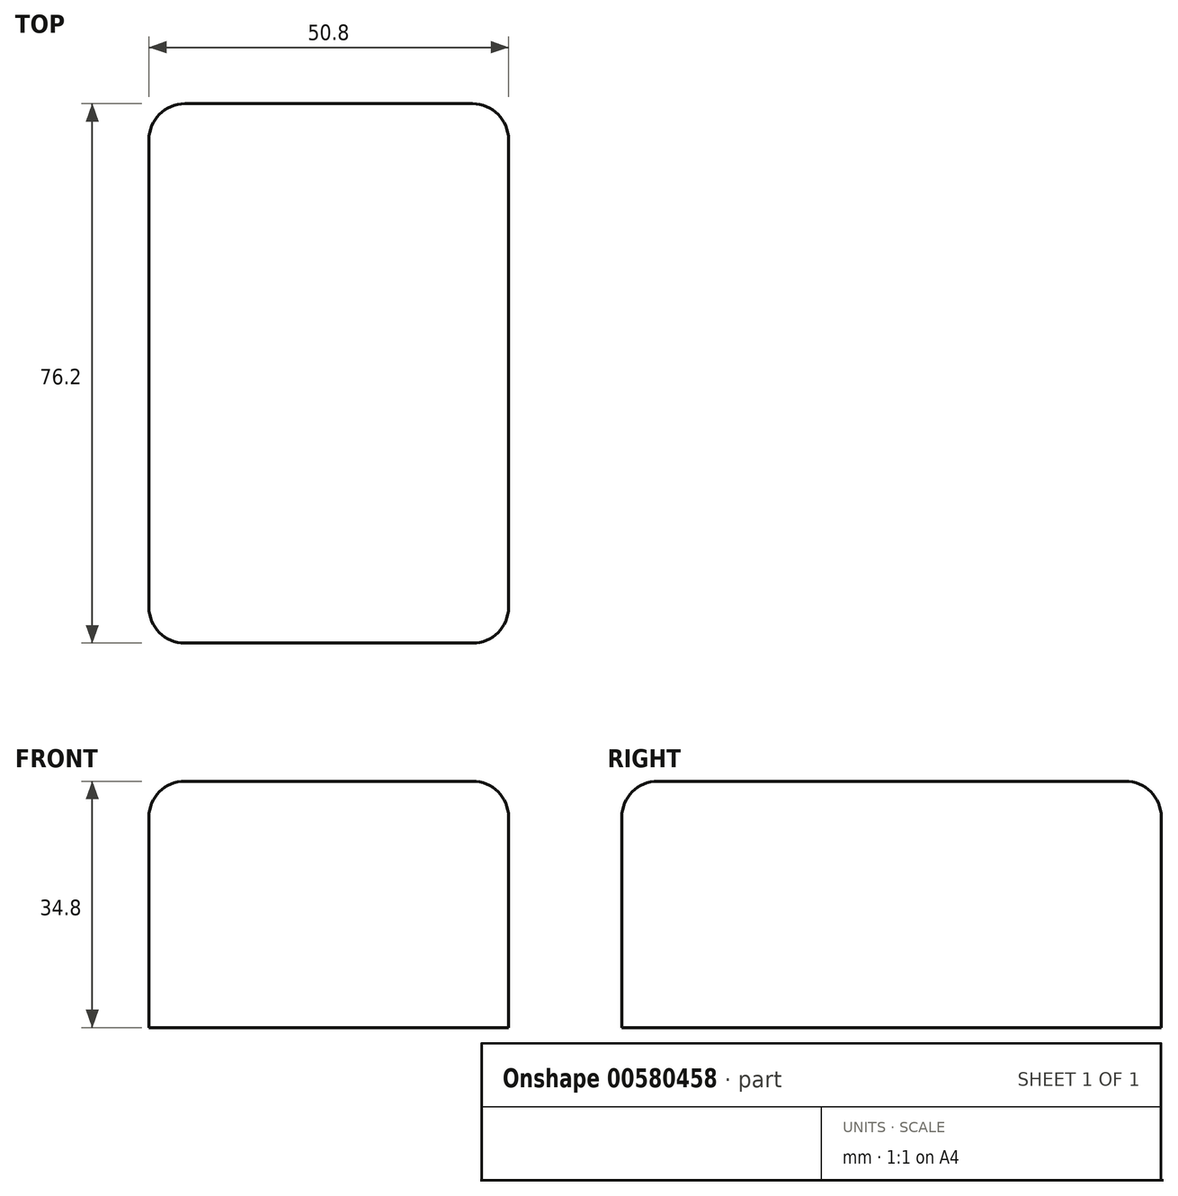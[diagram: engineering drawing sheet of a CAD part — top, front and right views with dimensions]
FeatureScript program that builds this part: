
annotation { "Feature Type Name" : "Feature", "Feature Type Description" : "" }
export const myFeature = defineFeature(function(context is Context, id is Id, definition is map)
    precondition{}
    {
        {
            var Q0;
            Q0=qCreatedBy(makeId("Top.planeOp"),FACE);
            var sketch = newSketch(context, id + "F0", { "sketchPlane" : qUnion([Q0])});
            skLineSegment(sketch, "E0.bottom", {"start": v(-25.4, 25.4) * mm, "end": v(25.4, 25.4) * mm});
            skLineSegment(sketch, "E0.top", {"start": v(-25.4, -50.8) * mm, "end": v(25.4, -50.8) * mm});
            skLineSegment(sketch, "E0.left", {"start": v(-25.4, 25.4) * mm, "end": v(-25.4, -50.8) * mm});
            skLineSegment(sketch, "E0.right", {"start": v(25.4, 25.4) * mm, "end": v(25.4, -50.8) * mm});
            skPoint(sketch, "E1.firstSnap0", {"position": v(0, 25.4) * mm});
            skSolve(sketch);
        }
        {
            var Q0;
            Q0=makeQuery(id+"F0.imprint","IMPRINT",FACE,{"disambiguationData":[TD([[makeQuery(id+"F0.imprint","IMPRINT",EDGE,{"derivedFrom":sQuery(id+"F0.wireOp",EDGE,"E0.bottom")}),-1.0]])]});
            extrude(context, id + "F1", {"entities" : qUnion([Q0]), "depth" : 34.8 * mm, "offsetDistance" : 25.4 * mm});
        }
        {
            var Q0;
            Q0=makeQuery(id+"F1.opExtrude","CAP_EDGE",EDGE,{"disambiguationData":[OSD([sQuery(id+"F0.wireOp",EDGE,"E0.left")])],"isStart":false});
            var Q1;
            Q1=makeQuery(id+"F1.opExtrude","CAP_EDGE",EDGE,{"disambiguationData":[OSD([sQuery(id+"F0.wireOp",EDGE,"E0.bottom")])],"isStart":false});
            var Q2;
            Q2=makeQuery(id+"F1.opExtrude","CAP_EDGE",EDGE,{"disambiguationData":[OSD([sQuery(id+"F0.wireOp",EDGE,"E0.right")])],"isStart":false});
            var Q3;
            Q3=makeQuery(id+"F1.opExtrude","CAP_FACE",FACE,{"disambiguationData":[OSD([sQuery(id+"F0.wireOp",EDGE,"E0.bottom"),sQuery(id+"F0.wireOp",EDGE,"E0.top"),sQuery(id+"F0.wireOp",EDGE,"E0.left"),sQuery(id+"F0.wireOp",EDGE,"E0.right")])],"isStart":false});
            var Q4;
            Q4=makeQuery(id+"F1.opExtrude","SWEPT_EDGE",EDGE,{"disambiguationData":[OSD([sQuery(id+"F0.wireOp",EDGE,"E0.top"),sQuery(id+"F0.wireOp",EDGE,"E0.right")])]});
            var Q5;
            Q5=makeQuery(id+"F1.opExtrude","SWEPT_EDGE",EDGE,{"disambiguationData":[OSD([sQuery(id+"F0.wireOp",EDGE,"E0.bottom"),sQuery(id+"F0.wireOp",EDGE,"E0.right")])]});
            var Q6;
            Q6=makeQuery(id+"F1.opExtrude","SWEPT_EDGE",EDGE,{"disambiguationData":[OSD([sQuery(id+"F0.wireOp",EDGE,"E0.bottom"),sQuery(id+"F0.wireOp",EDGE,"E0.left")])]});
            var Q7;
            Q7=makeQuery(id+"F1.opExtrude","SWEPT_EDGE",EDGE,{"disambiguationData":[OSD([sQuery(id+"F0.wireOp",EDGE,"E0.top"),sQuery(id+"F0.wireOp",EDGE,"E0.left")])]});
            fillet(context, id + "F2", {"entities" : qUnion([Q0, Q1, Q2, Q3, Q4, Q5, Q6, Q7]), "radius" : 5.08 * mm, "tangentPropagation" : true, "allowEdgeOverflow" : false});
        }
    });
